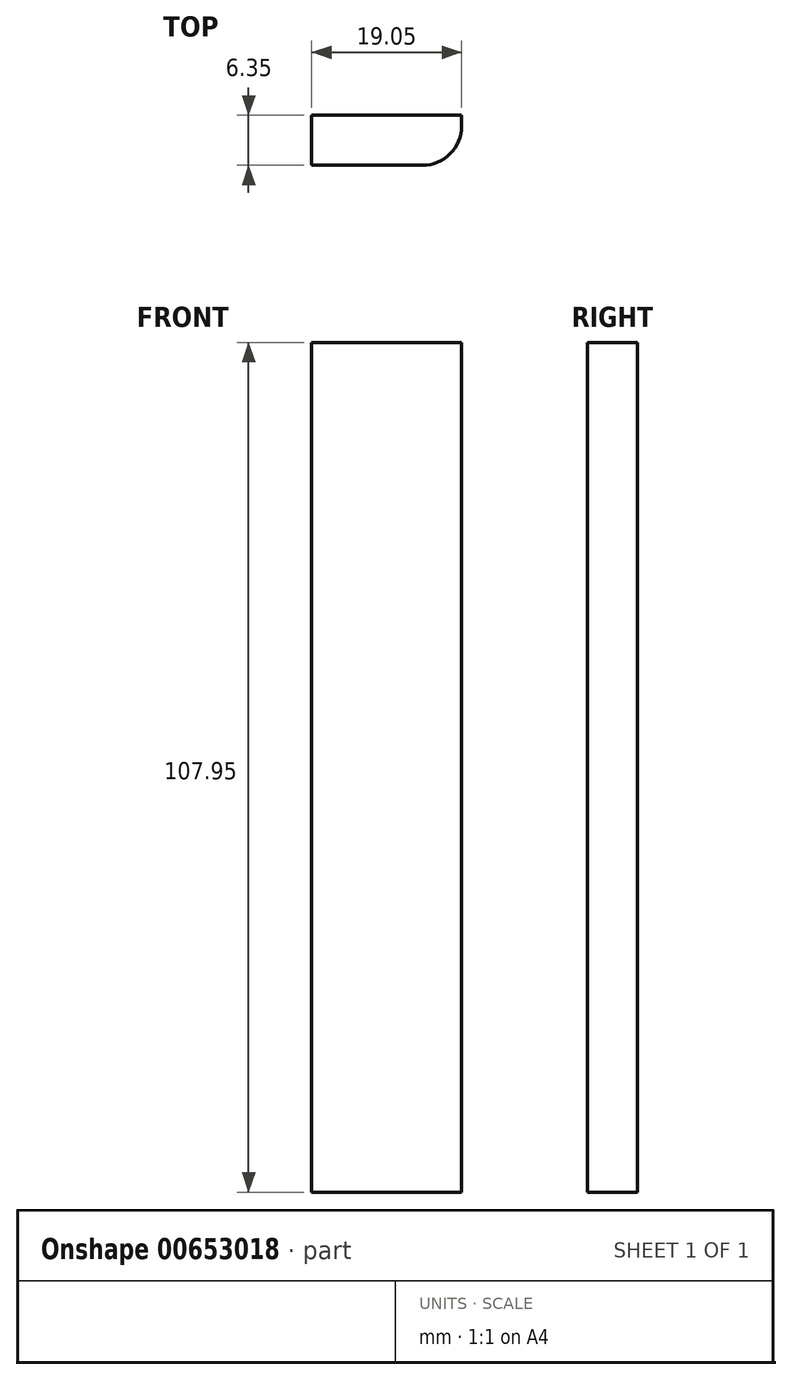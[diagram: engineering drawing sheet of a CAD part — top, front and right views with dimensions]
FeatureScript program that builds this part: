
annotation { "Feature Type Name" : "Feature", "Feature Type Description" : "" }
export const myFeature = defineFeature(function(context is Context, id is Id, definition is map)
    precondition{}
    {
        {
            var Q0;
            Q0=qCreatedBy(makeId("Front.planeOp"),FACE);
            var sketch = newSketch(context, id + "F0", { "sketchPlane" : qUnion([Q0])});
            skLineSegment(sketch, "E0.bottom", {"start": v(0, 0) * mm, "end": v(-19.05, 0) * mm});
            skLineSegment(sketch, "E0.top", {"start": v(0, 107.95) * mm, "end": v(-19.05, 107.95) * mm});
            skLineSegment(sketch, "E0.left", {"start": v(0, 0) * mm, "end": v(0, 107.95) * mm});
            skLineSegment(sketch, "E0.right", {"start": v(-19.05, 0) * mm, "end": v(-19.05, 107.95) * mm});
            skSolve(sketch);
        }
        {
            var Q0;
            Q0 = qSketchRegion(id + "F0", true);
            extrude(context, id + "F1", {"entities" : qUnion([Q0]), "depth" : 6.35 * mm, "offsetDistance" : 25 * mm});
        }
        {
            var Q0;
            Q0=makeQuery(id+"F1.opExtrude","CAP_EDGE",EDGE,{"disambiguationData":[OSD([sQuery(id+"F0.wireOp",EDGE,"E0.left")])],"isStart":false});
            fillet(context, id + "F2", {"entities" : qUnion([Q0]), "radius" : 5 * mm, "tangentPropagation" : true, "allowEdgeOverflow" : false});
        }
    });
